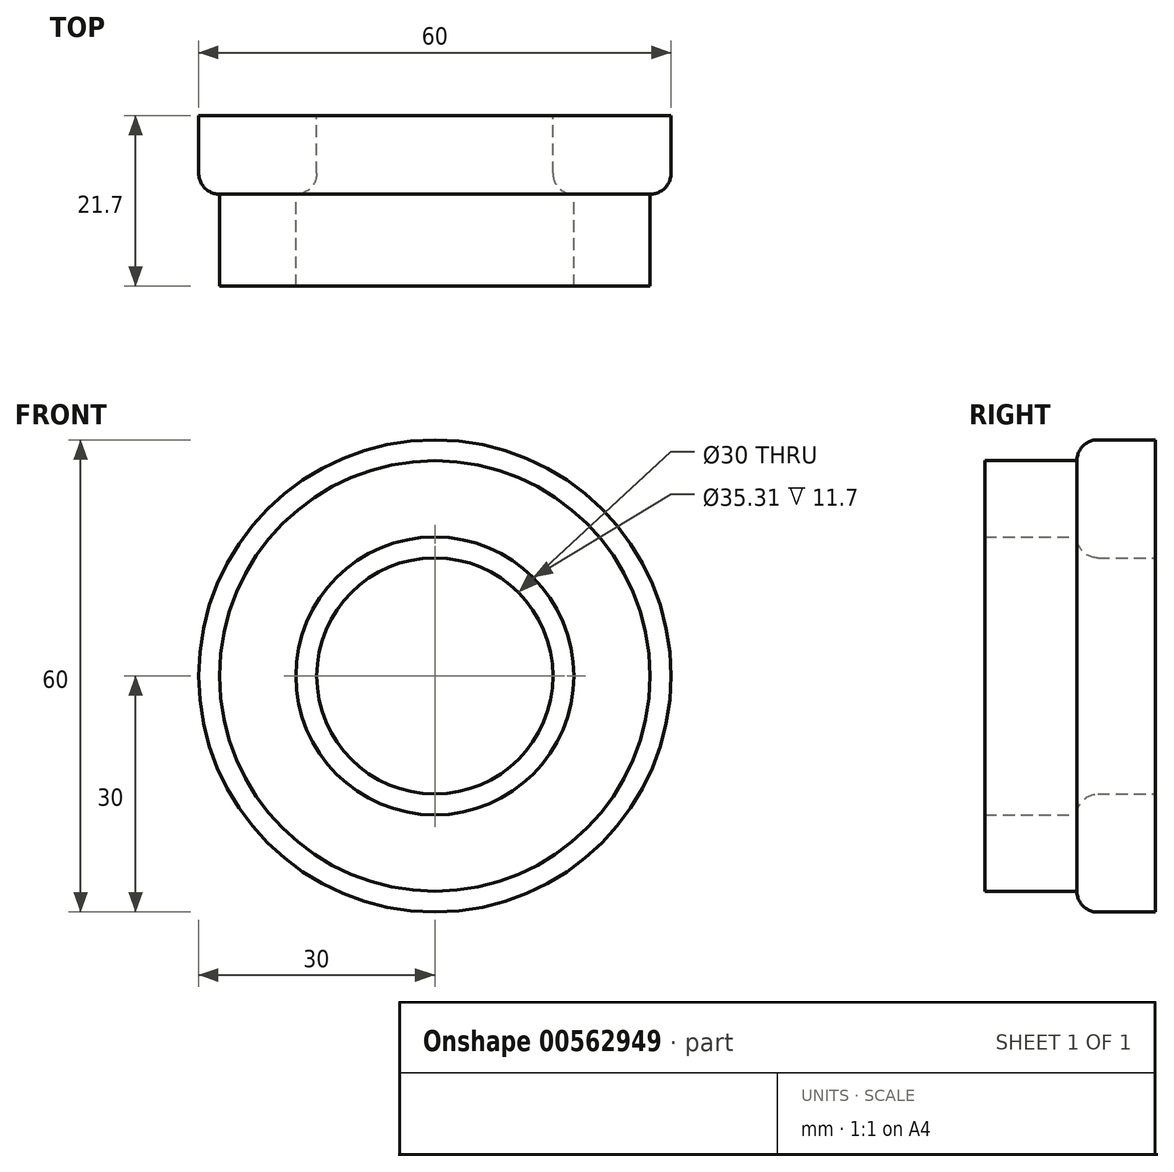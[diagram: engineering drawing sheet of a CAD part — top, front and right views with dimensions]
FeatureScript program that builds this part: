
annotation { "Feature Type Name" : "Feature", "Feature Type Description" : "" }
export const myFeature = defineFeature(function(context is Context, id is Id, definition is map)
    precondition{}
    {
        {
            var Q0;
            Q0=qCreatedBy(makeId("Front.planeOp"),FACE);
            var sketch = newSketch(context, id + "F0", { "sketchPlane" : qUnion([Q0])});
            skCircle(sketch, "E0", {"center": v(0, 0) * mm, "radius": 30 * mm});
            skCircle(sketch, "E1", {"center": v(0, 0) * mm, "radius": 15 * mm});
            skSolve(sketch);
        }
        {
            var Q0;
            Q0 = qSketchRegion(id + "F0", true);
            extrude(context, id + "F1", {"entities" : qUnion([Q0]), "depth" : 5 * mm, "offsetDistance" : 25 * mm, "hasSecondDirection" : true, "secondDirectionOppositeDirection" : true, "secondDirectionDepth" : 5 * mm});
        }
        {
            var Q0;
            Q0=makeQuery(id+"F1.opExtrude","CAP_FACE",FACE,{"disambiguationData":[OSD([sQuery(id+"F0.wireOp",EDGE,"E0"),sQuery(id+"F0.wireOp",EDGE,"E1")])],"isStart":false});
            fillet(context, id + "F2", {"entities" : qUnion([Q0]), "tangentPropagation" : true, "radius" : 2.66 * mm, "defaultsChanged" : false, "vertexSettings" : [], "allowEdgeOverflow" : false});
        }
        {
            var Q0;
            Q0=makeQuery(id+"F1.opExtrude","CAP_FACE",FACE,{"disambiguationData":[OSD([sQuery(id+"F0.wireOp",EDGE,"E0"),sQuery(id+"F0.wireOp",EDGE,"E1")])],"isStart":false});
            extrude(context, id + "F3", {"entities" : qUnion([Q0]), "operationType" : NewBodyOperationType.ADD, "depth" : 11.7 * mm, "offsetDistance" : 25 * mm});
        }
    });
